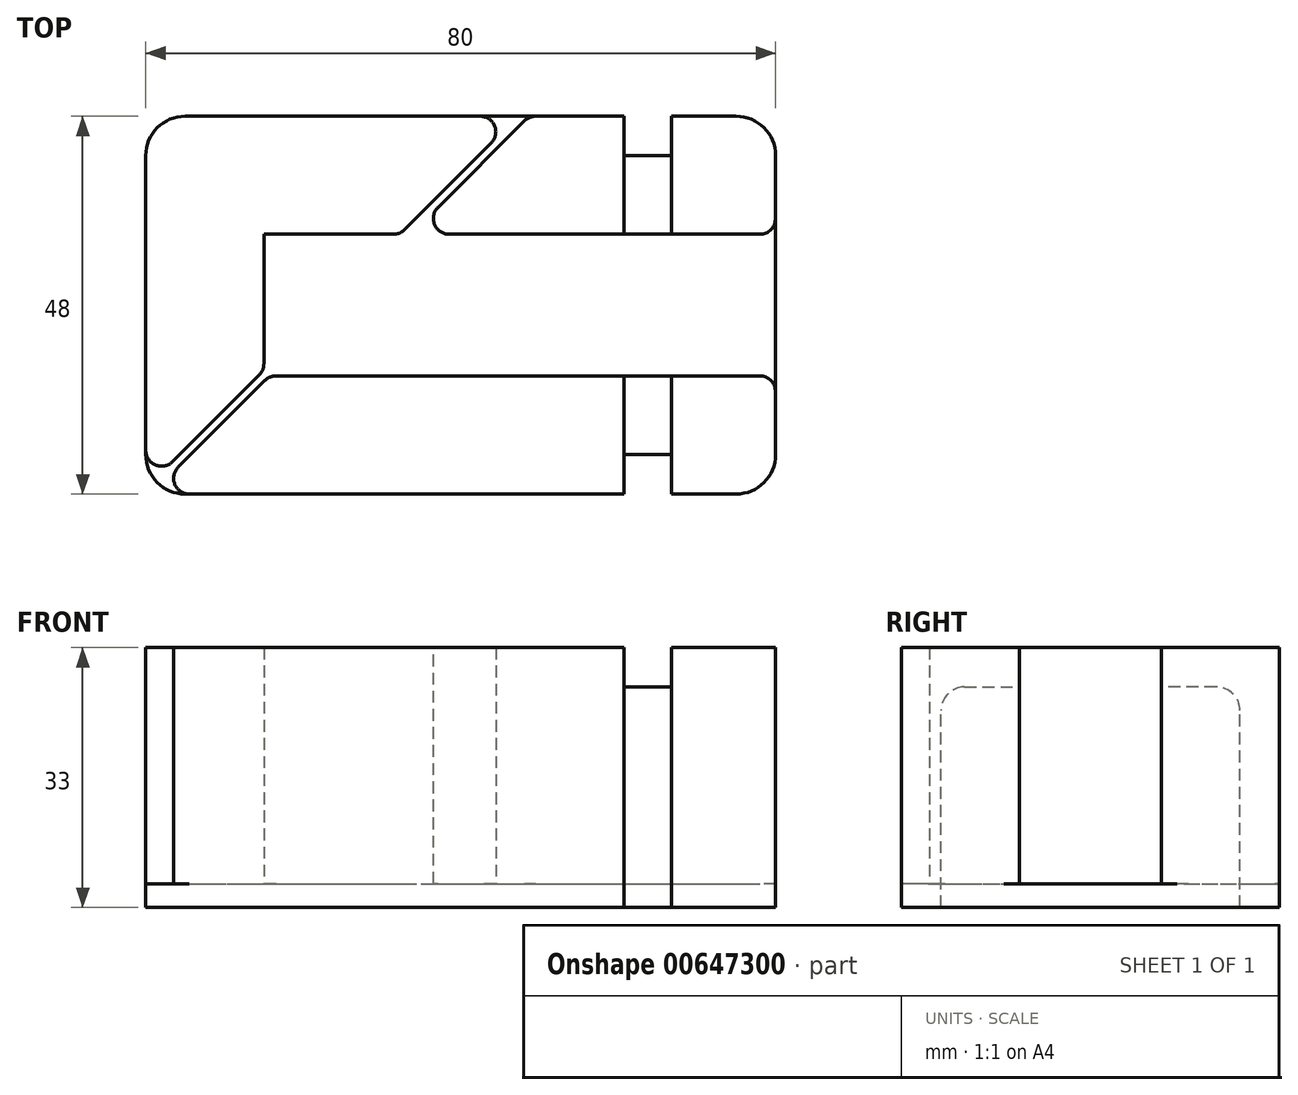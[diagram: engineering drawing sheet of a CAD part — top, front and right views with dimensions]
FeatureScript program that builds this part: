
annotation { "Feature Type Name" : "Feature", "Feature Type Description" : "" }
export const myFeature = defineFeature(function(context is Context, id is Id, definition is map)
    precondition{}
    {
        {
            var Q0;
            Q0=qCreatedBy(makeId("Top.planeOp"),FACE);
            var sketch = newSketch(context, id + "F0", { "sketchPlane" : qUnion([Q0])});
            skLineSegment(sketch, "E0.bottom", {"start": v(-48.04, -9) * mm, "end": v(16.25, -9) * mm});
            skLineSegment(sketch, "E0.top", {"start": v(-48.75, 9) * mm, "end": v(-31.46, 9) * mm});
            skLineSegment(sketch, "E0.left", {"start": v(-48.75, -8.3) * mm, "end": v(-48.75, 9) * mm});
            skLineSegment(sketch, "E0.right", {"start": v(16.25, -9) * mm, "end": v(16.25, 9) * mm});
            skPoint(sketch, "E0.middle", {"position": v(-16.25, 0) * mm});
            skLineSegment(sketch, "E1.0", {"start": v(-63.75, 24) * mm, "end": v(16.25, 24) * mm});
            skLineSegment(sketch, "E1.1", {"start": v(-63.75, -24) * mm, "end": v(-63.75, 24) * mm});
            skLineSegment(sketch, "E1.2", {"start": v(-63.75, -24) * mm, "end": v(16.25, -24) * mm});
            skLineSegment(sketch, "E2", {"start": v(16.25, -24) * mm, "end": v(16.25, -9) * mm});
            skLineSegment(sketch, "E3", {"start": v(16.25, 9) * mm, "end": v(16.25, 24) * mm});
            skLineSegment(sketch, "E4", {"start": v(-63.75, -23.3) * mm, "end": v(-48.75, -8.3) * mm});
            skLineSegment(sketch, "E5", {"start": v(-63.04, -24) * mm, "end": v(-48.04, -9) * mm});
            skLineSegment(sketch, "E6", {"start": v(-49.1, -8.65) * mm, "end": v(-48.4, -9.35) * mm, "construction": true});
            skLineSegment(sketch, "E7.trimOffspring", {"start": v(-30.04, 9) * mm, "end": v(16.25, 9) * mm});
            skPoint(sketch, "E8.orphan", {"position": v(-48.75, -9) * mm});
            skLineSegment(sketch, "E9.trimOffspring", {"start": v(-30.04, 9) * mm, "end": v(-15.04, 24) * mm});
            skLineSegment(sketch, "E10.trimOffspring", {"start": v(-31.46, 9) * mm, "end": v(-16.46, 24) * mm});
            skLineSegment(sketch, "E11", {"start": v(-16.25, 0) * mm, "end": v(16.25, 0) * mm, "construction": true});
            skSolve(sketch);
        }
        {
            var Q0;
            Q0=makeQuery(id+"F0.imprint","IMPRINT",FACE,{"disambiguationData":[TD([[makeQuery(id+"F0.imprint","IMPRINT",EDGE,{"derivedFrom":sQuery(id+"F0.wireOp",EDGE,"E0.bottom")}),1.0]])]});
            var Q1;
            Q1=makeQuery(id+"F0.imprint","IMPRINT",FACE,{"disambiguationData":[TD([[makeQuery(id+"F0.imprint","IMPRINT",EDGE,{"derivedFrom":sQuery(id+"F0.wireOp",EDGE,"E0.top")}),1.0]])]});
            var Q2;
            {var subQ0=sQuery(id+"F0.wireOp",EDGE,"E3");Q2=makeQuery(id+"F0.imprint","IMPRINT",FACE,{"disambiguationData":[TD([[makeQuery(id+"F0.imprint","IMPRINT",EDGE,{"derivedFrom":subQ0}),1.0]])]});}
            var Q3;
            Q3=makeQuery(id+"F0.imprint","IMPRINT",FACE,{"disambiguationData":[TD([[makeQuery(id+"F0.imprint","IMPRINT",EDGE,{"derivedFrom":sQuery(id+"F0.wireOp",EDGE,"E0.bottom")}),-1.0]])]});
            extrude(context, id + "F1", {"entities" : qUnion([Q0, Q1, Q2, Q3]), "oppositeDirection" : true, "depth" : 3 * mm, "offsetDistance" : 25 * mm});
        }
        {
            var Q0;
            Q0=makeQuery(id+"F0.imprint","IMPRINT",FACE,{"disambiguationData":[TD([[makeQuery(id+"F0.imprint","IMPRINT",EDGE,{"derivedFrom":sQuery(id+"F0.wireOp",EDGE,"E0.top")}),1.0]])]});
            var Q1;
            {var subQ0=sQuery(id+"F0.wireOp",EDGE,"E3");Q1=makeQuery(id+"F0.imprint","IMPRINT",FACE,{"disambiguationData":[TD([[makeQuery(id+"F0.imprint","IMPRINT",EDGE,{"derivedFrom":subQ0}),1.0]])]});}
            var Q2;
            Q2=makeQuery(id+"F0.imprint","IMPRINT",FACE,{"disambiguationData":[TD([[makeQuery(id+"F0.imprint","IMPRINT",EDGE,{"derivedFrom":sQuery(id+"F0.wireOp",EDGE,"E0.bottom")}),-1.0]])]});
            extrude(context, id + "F2", {"entities" : qUnion([Q0, Q1, Q2]), "operationType" : NewBodyOperationType.ADD, "depth" : 30 * mm, "offsetDistance" : 25 * mm});
        }
        {
            var Q0;
            Q0=makeQuery(id+"F1.opExtrude","CAP_FACE",FACE,{"disambiguationData":[OSD([sQuery(id+"F0.wireOp",EDGE,"E0.right"),sQuery(id+"F0.wireOp",EDGE,"E1.0"),sQuery(id+"F0.wireOp",EDGE,"E1.1"),sQuery(id+"F0.wireOp",EDGE,"E1.2"),sQuery(id+"F0.wireOp",EDGE,"E2"),sQuery(id+"F0.wireOp",EDGE,"E3")])],"isStart":false});
            var sketch = newSketch(context, id + "F3", { "sketchPlane" : qUnion([Q0])});
            skLineSegment(sketch, "E12", {"start": v(0, -24) * mm, "end": v(0, 24) * mm, "construction": true});
            skLineSegment(sketch, "E13.bottom", {"start": v(3, -29) * mm, "end": v(-3, -29) * mm});
            skLineSegment(sketch, "E13.top", {"start": v(3, -19) * mm, "end": v(-3, -19) * mm});
            skLineSegment(sketch, "E13.left", {"start": v(3, -29) * mm, "end": v(3, -19) * mm});
            skLineSegment(sketch, "E13.right", {"start": v(-3, -29) * mm, "end": v(-3, -19) * mm});
            skPoint(sketch, "E13.middle", {"position": v(0, -24) * mm});
            skLineSegment(sketch, "E14.MirrorCS", {"start": v(3, 19) * mm, "end": v(-3, 19) * mm});
            skLineSegment(sketch, "E15.MirrorCS", {"start": v(3, 29) * mm, "end": v(3, 19) * mm});
            skLineSegment(sketch, "E16.MirrorCS", {"start": v(3, 29) * mm, "end": v(-3, 29) * mm});
            skLineSegment(sketch, "E17.MirrorCS", {"start": v(-3, 29) * mm, "end": v(-3, 19) * mm});
            skSolve(sketch);
        }
        {
            var Q0;
            Q0=sQuery(id+"F0.wireOp",EDGE,"E11");
            cPoint(context, id + "F4", {"entities" : qUnion([Q0]), "parameter" : 0.5});
        }
        {
            var Q0;
            Q0 = qCreatedBy(id + "F4" ,VERTEX);
            var Q1;
            {var subQ0=sQuery(id+"F0.wireOp",EDGE,"E3");var subQ1=sQuery(id+"F0.wireOp",EDGE,"E2");Q1=makeQuery(id+"F2.boolean.opBoolean","MERGE",FACE,{"derivedFrom":[makeQuery(id+"F1.opExtrude","SWEPT_FACE",FACE,{"disambiguationData":[OSD([sQuery(id+"F0.wireOp",EDGE,"E0.right"),subQ1,subQ0])]}),makeQuery(id+"F2.opExtrude","SWEPT_FACE",FACE,{"disambiguationData":[OSD([subQ1])]}),makeQuery(id+"F2.opExtrude","SWEPT_FACE",FACE,{"disambiguationData":[OSD([subQ0])]})]});}
            cPlane(context, id + "F5", {"entities" : qUnion([Q0, Q1]), "cplaneType" : CPlaneType.PLANE_POINT, "offset" : 25 * mm, "width" : 150 * mm, "height" : 150 * mm});
        }
        {
            var Q0;
            Q0=qCreatedBy(id+"F5.planeOp",FACE);
            var sketch = newSketch(context, id + "F6", { "sketchPlane" : qUnion([Q0])});
            skLineSegment(sketch, "E18", {"start": v(-9, 30) * mm, "end": v(-24, 30) * mm});
            skLineSegment(sketch, "E19", {"start": v(24, 30) * mm, "end": v(9, 30) * mm});
            skLineSegment(sketch, "E20", {"start": v(-24, 30) * mm, "end": v(-24, -3) * mm});
            skLineSegment(sketch, "E21", {"start": v(24, 30) * mm, "end": v(24, -3) * mm});
            skSolve(sketch);
        }
        {
            var Q0;
            {var subQ0=sQuery(id+"F3.wireOp",EDGE,"E14.MirrorCS");Q0=makeQuery(id+"F3.imprint","IMPRINT",FACE,{"disambiguationData":[TD([[makeQuery(id+"F3.imprint","IMPRINT",EDGE,{"derivedFrom":subQ0}),-1.0]])]});}
            var Q1;
            Q1=sQuery(id+"F6.wireOp",EDGE,"E20");
            var Q2;
            Q2=sQuery(id+"F6.wireOp",EDGE,"E18");
            sweep(context, id + "F7", {"operationType" : NewBodyOperationType.REMOVE, "profiles" : qUnion([Q0]), "path" : qUnion([Q1, Q2])});
        }
        {
            var Q0;
            {var subQ0=sQuery(id+"F3.wireOp",EDGE,"E13.top");Q0=makeQuery(id+"F3.imprint","IMPRINT",FACE,{"disambiguationData":[TD([[makeQuery(id+"F3.imprint","IMPRINT",EDGE,{"derivedFrom":subQ0}),1.0]])]});}
            var Q1;
            Q1=sQuery(id+"F6.wireOp",EDGE,"E21");
            var Q2;
            Q2=sQuery(id+"F6.wireOp",EDGE,"E19");
            sweep(context, id + "F8", {"operationType" : NewBodyOperationType.REMOVE, "profiles" : qUnion([Q0]), "path" : qUnion([Q1, Q2])});
        }
        {
            var Q0;
            Q0=makeQuery(id+"F7.boolean.opBoolean","COPY",EDGE,{"derivedFrom":makeQuery(id+"F7.opSweep","MID_CAP_EDGE",EDGE,{"disambiguationData":[OSD([sQuery(id+"F3.wireOp",EDGE,"E14.MirrorCS"),sQuery(id+"F6.wireOp",VERTEX,"E18.end")])],"capPos":1.0})});
            var Q1;
            Q1=makeQuery(id+"F8.boolean.opBoolean","COPY",EDGE,{"derivedFrom":makeQuery(id+"F8.opSweep","MID_CAP_EDGE",EDGE,{"disambiguationData":[OSD([sQuery(id+"F3.wireOp",EDGE,"E13.top"),sQuery(id+"F6.wireOp",VERTEX,"E19.start")])],"capPos":1.0})});
            var Q2;
            Q2=makeQuery(id+"F7.boolean.opBoolean","COPY",EDGE,{"derivedFrom":makeQuery(id+"F7.opSweep","CAP_EDGE",EDGE,{"disambiguationData":[OSD([sQuery(id+"F3.wireOp",EDGE,"E14.MirrorCS"),sQuery(id+"F6.wireOp",VERTEX,"E18.start")])],"isStart":false})});
            var Q3;
            Q3=makeQuery(id+"F8.boolean.opBoolean","COPY",EDGE,{"derivedFrom":makeQuery(id+"F8.opSweep","CAP_EDGE",EDGE,{"disambiguationData":[OSD([sQuery(id+"F3.wireOp",EDGE,"E13.top"),sQuery(id+"F6.wireOp",VERTEX,"E19.end")])],"isStart":false})});
            var Q4;
            Q4=makeQuery(id+"F7.boolean.opBoolean","COPY",EDGE,{"derivedFrom":makeQuery(id+"F7.opSweep","CAP_EDGE",EDGE,{"disambiguationData":[OSD([sQuery(id+"F3.wireOp",EDGE,"E14.MirrorCS"),sQuery(id+"F6.wireOp",VERTEX,"E20.end")])],"isStart":true})});
            var Q5;
            Q5=makeQuery(id+"F8.boolean.opBoolean","COPY",EDGE,{"derivedFrom":makeQuery(id+"F8.opSweep","CAP_EDGE",EDGE,{"disambiguationData":[OSD([sQuery(id+"F3.wireOp",EDGE,"E13.top"),sQuery(id+"F6.wireOp",VERTEX,"E21.end")])],"isStart":true})});
            fillet(context, id + "F9", {"entities" : qUnion([Q0, Q1, Q2, Q3, Q4, Q5]), "radius" : 3 * mm, "tangentPropagation" : true, "allowEdgeOverflow" : false});
        }
        {
            var Q0;
            Q0=makeQuery(id+"F2.opExtrude","SWEPT_EDGE",EDGE,{"disambiguationData":[OSD([sQuery(id+"F0.wireOp",EDGE,"E1.1"),sQuery(id+"F0.wireOp",EDGE,"E4")])]});
            var Q1;
            Q1=makeQuery(id+"F2.opExtrude","SWEPT_EDGE",EDGE,{"disambiguationData":[OSD([sQuery(id+"F0.wireOp",EDGE,"E1.2"),sQuery(id+"F0.wireOp",EDGE,"E5")])]});
            var Q2;
            Q2=makeQuery(id+"F2.opExtrude","SWEPT_EDGE",EDGE,{"disambiguationData":[OSD([sQuery(id+"F0.wireOp",EDGE,"E0.left"),sQuery(id+"F0.wireOp",EDGE,"E4")])]});
            var Q3;
            Q3=makeQuery(id+"F2.opExtrude","SWEPT_EDGE",EDGE,{"disambiguationData":[OSD([sQuery(id+"F0.wireOp",EDGE,"E0.bottom"),sQuery(id+"F0.wireOp",EDGE,"E5")])]});
            var Q4;
            Q4=makeQuery(id+"F2.opExtrude","SWEPT_EDGE",EDGE,{"disambiguationData":[OSD([sQuery(id+"F0.wireOp",EDGE,"E0.top"),sQuery(id+"F0.wireOp",EDGE,"E10.trimOffspring")])]});
            var Q5;
            Q5=makeQuery(id+"F2.opExtrude","SWEPT_EDGE",EDGE,{"disambiguationData":[OSD([sQuery(id+"F0.wireOp",EDGE,"E7.trimOffspring"),sQuery(id+"F0.wireOp",EDGE,"E9.trimOffspring")])]});
            var Q6;
            Q6=makeQuery(id+"F2.opExtrude","SWEPT_EDGE",EDGE,{"disambiguationData":[OSD([sQuery(id+"F0.wireOp",EDGE,"E1.0"),sQuery(id+"F0.wireOp",EDGE,"E10.trimOffspring")])]});
            var Q7;
            Q7=makeQuery(id+"F2.opExtrude","SWEPT_EDGE",EDGE,{"disambiguationData":[OSD([sQuery(id+"F0.wireOp",EDGE,"E1.0"),sQuery(id+"F0.wireOp",EDGE,"E9.trimOffspring")])]});
            var Q8;
            Q8=makeQuery(id+"F2.opExtrude","SWEPT_EDGE",EDGE,{"disambiguationData":[OSD([sQuery(id+"F0.wireOp",EDGE,"E0.right"),sQuery(id+"F0.wireOp",EDGE,"E3"),sQuery(id+"F0.wireOp",EDGE,"E7.trimOffspring")])]});
            var Q9;
            Q9=makeQuery(id+"F2.opExtrude","SWEPT_EDGE",EDGE,{"disambiguationData":[OSD([sQuery(id+"F0.wireOp",EDGE,"E0.bottom"),sQuery(id+"F0.wireOp",EDGE,"E0.right"),sQuery(id+"F0.wireOp",EDGE,"E2")])]});
            var Q10;
            Q10=makeQuery(id+"F8.boolean.opBoolean","COPY",EDGE,{"derivedFrom":makeQuery(id+"F8.opSweep","CAP_EDGE",EDGE,{"disambiguationData":[OSD([sQuery(id+"F3.wireOp",EDGE,"E13.right"),sQuery(id+"F6.wireOp",VERTEX,"E19.end")])],"isStart":false})});
            var Q11;
            Q11=makeQuery(id+"F8.boolean.opBoolean","COPY",EDGE,{"derivedFrom":makeQuery(id+"F8.opSweep","CAP_EDGE",EDGE,{"disambiguationData":[OSD([sQuery(id+"F3.wireOp",EDGE,"E13.left"),sQuery(id+"F6.wireOp",VERTEX,"E19.end")])],"isStart":false})});
            var Q12;
            Q12=makeQuery(id+"F8.boolean.opBoolean","COPY",EDGE,{"derivedFrom":makeQuery(id+"F8.opSweep","SWEPT_EDGE",EDGE,{"disambiguationData":[OSD([sQuery(id+"F0.wireOp",EDGE,"E1.0"),sQuery(id+"F3.wireOp",EDGE,"E13.right"),sQuery(id+"F6.wireOp",EDGE,"E21")])]})});
            var Q13;
            Q13=makeQuery(id+"F8.boolean.opBoolean","COPY",EDGE,{"derivedFrom":makeQuery(id+"F8.opSweep","SWEPT_EDGE",EDGE,{"disambiguationData":[OSD([sQuery(id+"F0.wireOp",EDGE,"E1.0"),sQuery(id+"F3.wireOp",EDGE,"E13.left"),sQuery(id+"F6.wireOp",EDGE,"E21")])]})});
            var Q14;
            Q14=makeQuery(id+"F7.boolean.opBoolean","COPY",EDGE,{"derivedFrom":makeQuery(id+"F7.opSweep","SWEPT_EDGE",EDGE,{"disambiguationData":[OSD([sQuery(id+"F0.wireOp",EDGE,"E1.2"),sQuery(id+"F3.wireOp",EDGE,"E17.MirrorCS"),sQuery(id+"F6.wireOp",EDGE,"E20")])]})});
            var Q15;
            Q15=makeQuery(id+"F7.boolean.opBoolean","COPY",EDGE,{"derivedFrom":makeQuery(id+"F7.opSweep","SWEPT_EDGE",EDGE,{"disambiguationData":[OSD([sQuery(id+"F0.wireOp",EDGE,"E1.2"),sQuery(id+"F3.wireOp",EDGE,"E15.MirrorCS"),sQuery(id+"F6.wireOp",EDGE,"E20")])]})});
            var Q16;
            Q16=makeQuery(id+"F7.boolean.opBoolean","COPY",EDGE,{"derivedFrom":makeQuery(id+"F7.opSweep","CAP_EDGE",EDGE,{"disambiguationData":[OSD([sQuery(id+"F3.wireOp",EDGE,"E17.MirrorCS"),sQuery(id+"F6.wireOp",VERTEX,"E18.start")])],"isStart":false})});
            var Q17;
            Q17=makeQuery(id+"F7.boolean.opBoolean","COPY",EDGE,{"derivedFrom":makeQuery(id+"F7.opSweep","CAP_EDGE",EDGE,{"disambiguationData":[OSD([sQuery(id+"F3.wireOp",EDGE,"E15.MirrorCS"),sQuery(id+"F6.wireOp",VERTEX,"E18.start")])],"isStart":false})});
            var Q18;
            Q18=makeQuery(id+"F11.opFillet","BLEND_EDGE",EDGE,{"blendedFrom":[makeQuery(id+"F1.opExtrude","SWEPT_EDGE",EDGE,{"disambiguationData":[OSD([sQuery(id+"F0.wireOp",EDGE,"E1.1"),sQuery(id+"F0.wireOp",EDGE,"E1.2")])]}),makeQuery(id+"F2.opExtrude","SWEPT_FACE",FACE,{"disambiguationData":[OSD([sQuery(id+"F0.wireOp",EDGE,"E4")])]})],"blendedInto":[makeQuery(id+"F2.opExtrude","SWEPT_FACE",FACE,{"disambiguationData":[OSD([sQuery(id+"F0.wireOp",EDGE,"E4")])]})]});
            var Q19;
            Q19=makeQuery(id+"F11.opFillet","BLEND_EDGE",EDGE,{"blendedFrom":[makeQuery(id+"F1.opExtrude","SWEPT_EDGE",EDGE,{"disambiguationData":[OSD([sQuery(id+"F0.wireOp",EDGE,"E1.1"),sQuery(id+"F0.wireOp",EDGE,"E1.2")])]}),makeQuery(id+"F2.opExtrude","SWEPT_FACE",FACE,{"disambiguationData":[OSD([sQuery(id+"F0.wireOp",EDGE,"E5")])]})],"blendedInto":[makeQuery(id+"F2.opExtrude","SWEPT_FACE",FACE,{"disambiguationData":[OSD([sQuery(id+"F0.wireOp",EDGE,"E5")])]})]});
            fillet(context, id + "F10", {"entities" : qUnion([Q0, Q1, Q2, Q3, Q4, Q5, Q6, Q7, Q8, Q9, Q10, Q11, Q12, Q13, Q14, Q15, Q16, Q17, Q18, Q19]), "radius" : 2 * mm, "tangentPropagation" : true, "allowEdgeOverflow" : false});
        }
        {
            var Q0;
            {var subQ0=sQuery(id+"F0.wireOp",EDGE,"E2");var subQ1=sQuery(id+"F0.wireOp",EDGE,"E1.2");Q0=makeQuery(id+"F2.boolean.opBoolean","MERGE",EDGE,{"derivedFrom":[makeQuery(id+"F1.opExtrude","SWEPT_EDGE",EDGE,{"disambiguationData":[OSD([subQ1,subQ0])]}),makeQuery(id+"F2.opExtrude","SWEPT_EDGE",EDGE,{"disambiguationData":[OSD([subQ1,subQ0])]})]});}
            var Q1;
            {var subQ0=sQuery(id+"F0.wireOp",EDGE,"E3");var subQ1=sQuery(id+"F0.wireOp",EDGE,"E1.0");Q1=makeQuery(id+"F2.boolean.opBoolean","MERGE",EDGE,{"derivedFrom":[makeQuery(id+"F1.opExtrude","SWEPT_EDGE",EDGE,{"disambiguationData":[OSD([subQ1,subQ0])]}),makeQuery(id+"F2.opExtrude","SWEPT_EDGE",EDGE,{"disambiguationData":[OSD([subQ1,subQ0])]})]});}
            var Q2;
            {var subQ0=sQuery(id+"F0.wireOp",EDGE,"E1.1");var subQ1=sQuery(id+"F0.wireOp",EDGE,"E1.0");Q2=makeQuery(id+"F2.boolean.opBoolean","MERGE",EDGE,{"derivedFrom":[makeQuery(id+"F1.opExtrude","SWEPT_EDGE",EDGE,{"disambiguationData":[OSD([subQ1,subQ0])]}),makeQuery(id+"F2.opExtrude","SWEPT_EDGE",EDGE,{"disambiguationData":[OSD([subQ1,subQ0])]})]});}
            var Q3;
            Q3=makeQuery(id+"F1.opExtrude","SWEPT_EDGE",EDGE,{"disambiguationData":[OSD([sQuery(id+"F0.wireOp",EDGE,"E1.1"),sQuery(id+"F0.wireOp",EDGE,"E1.2")])]});
            fillet(context, id + "F11", {"entities" : qUnion([Q0, Q1, Q2, Q3]), "radius" : 5 * mm, "tangentPropagation" : true, "allowEdgeOverflow" : false});
        }
    });
